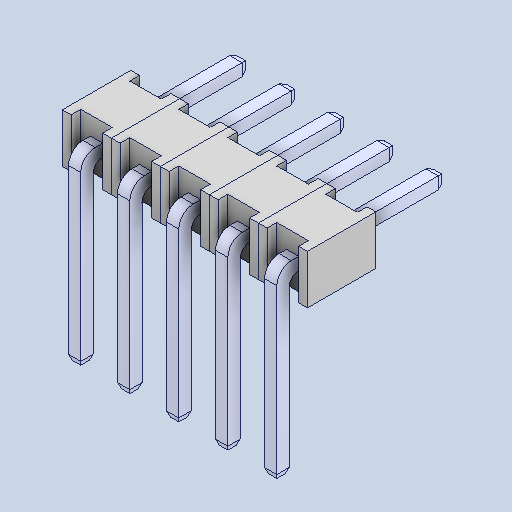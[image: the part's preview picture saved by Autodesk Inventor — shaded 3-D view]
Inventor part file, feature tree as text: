
AUTODESK INVENTOR PART (.ipt)
format: ipt  version: 2022 (Build 260153000, 153)  size: 239,616 bytes
history: mixed  units: mm
features: other x4, chamfer x1, imported_body x1
ambient origin geometry x8: Origin, YZ Plane, XZ Plane, XY Plane, X Axis, Y Axis, Z Axis, Center Point
bodies: Solid1 (imported_parasolid), Solid2 (imported_parasolid), Solid3 (imported_parasolid), Solid4 (imported_parasolid), Solid5 (imported_parasolid)
feature tree (6):
  chamfer  "Chamfer2"  [1 undecoded]
  other  "Num pins[1]"
  other  "Num pins[2]"
  other  "Num pins[3]"
  other  "Num pins[4]"
  imported_body  NMx_Import_Brep_tag  [imported B-rep: ~175 faces, bbox_mm=[12.7, 10.4525, 8.635]]
note: 1 required parameter value undecoded (feature->parameter linkage not recoverable at this tier; creation-order binding heuristic only, values carry confidence <= 0.55)
